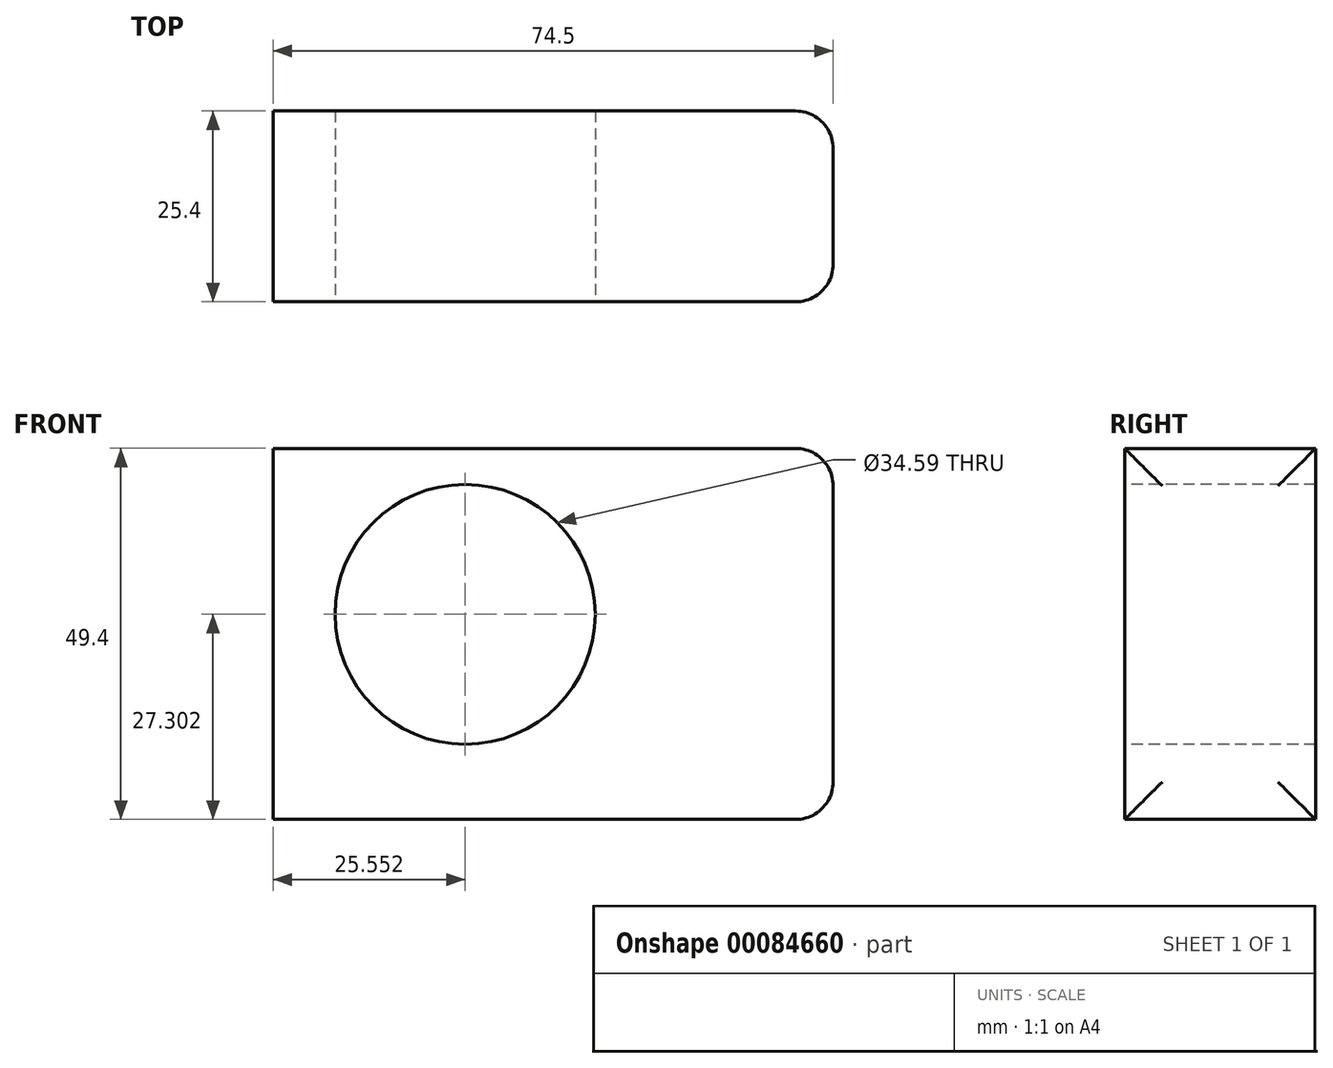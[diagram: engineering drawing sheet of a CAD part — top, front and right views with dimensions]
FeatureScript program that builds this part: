
annotation { "Feature Type Name" : "Feature", "Feature Type Description" : "" }
export const myFeature = defineFeature(function(context is Context, id is Id, definition is map)
    precondition{}
    {
        {
            var Q0;
            Q0=qCreatedBy(makeId("Front.planeOp"),FACE);
            var sketch = newSketch(context, id + "F4", { "sketchPlane" : qUnion([Q0])});
            skLineSegment(sketch, "E0.bottom", {"start": v(32.17, 49.4) * mm, "end": v(-42.33, 49.4) * mm});
            skLineSegment(sketch, "E0.top", {"start": v(32.17, 0) * mm, "end": v(-42.33, 0) * mm});
            skLineSegment(sketch, "E0.left", {"start": v(32.17, 49.4) * mm, "end": v(32.17, 0) * mm});
            skLineSegment(sketch, "E0.right", {"start": v(-42.33, 49.4) * mm, "end": v(-42.33, 0) * mm});
            skSolve(sketch);
        }
        {
            var Q0;
            Q0=makeQuery(id+"F4.imprint","IMPRINT",FACE,{"disambiguationData":[TD([[makeQuery(id+"F4.imprint","IMPRINT",EDGE,{"derivedFrom":sQuery(id+"F4.wireOp",EDGE,"E0.bottom")}),1.0]])]});
            extrude(context, id + "F5", {"entities" : qUnion([Q0]), "depth" : 25.4 * mm});
        }
        {
            var Q0;
            Q0=makeQuery(id+"F5.opExtrude","CAP_FACE",FACE,{"disambiguationData":[OSD([sQuery(id+"F4.wireOp",EDGE,"E0.bottom"),sQuery(id+"F4.wireOp",EDGE,"E0.top"),sQuery(id+"F4.wireOp",EDGE,"E0.left"),sQuery(id+"F4.wireOp",EDGE,"E0.right")])],"isStart":false});
            var sketch = newSketch(context, id + "F0", { "sketchPlane" : qUnion([Q0])});
            skSolve(sketch);
        }
        {
            var Q0;
            Q0=makeQuery(id+"F0.imprint","IMPRINT",FACE,{"disambiguationData":[TD([[makeQuery(id+"F0.imprint","IMPRINT",EDGE,{"derivedFrom":makeQuery(id+"F5.opExtrude","CAP_EDGE",EDGE,{"disambiguationData":[OSD([sQuery(id+"F4.wireOp",EDGE,"E0.bottom")])],"isStart":false})}),1.0]])]});
            var sketch = newSketch(context, id + "F6", { "sketchPlane" : qUnion([Q0])});
            skCircle(sketch, "E1", {"center": v(-16.78, 27.3) * mm, "radius": 17.3 * mm});
            skSolve(sketch);
        }
        {
            var Q0;
            Q0=makeQuery(id+"F6.imprint","IMPRINT",FACE,{"disambiguationData":[TD([[makeQuery(id+"F6.imprint","IMPRINT",EDGE,{"derivedFrom":sQuery(id+"F6.wireOp",EDGE,"E1")}),-1.0]])]});
            var sketch = newSketch(context, id + "F7", { "sketchPlane" : qUnion([Q0])});
            skSolve(sketch);
        }
        {
            var Q0;
            Q0=makeQuery(id+"F5.opExtrude","SWEPT_EDGE",EDGE,{"disambiguationData":[OSD([sQuery(id+"F4.wireOp",EDGE,"E0.bottom"),sQuery(id+"F4.wireOp",EDGE,"E0.left")])]});
            var Q1;
            Q1=makeQuery(id+"F5.opExtrude","CAP_EDGE",EDGE,{"disambiguationData":[OSD([sQuery(id+"F4.wireOp",EDGE,"E0.left")])],"isStart":true});
            var Q2;
            Q2=makeQuery(id+"F5.opExtrude","CAP_EDGE",EDGE,{"disambiguationData":[OSD([sQuery(id+"F4.wireOp",EDGE,"E0.left")])],"isStart":false});
            var Q3;
            Q3=makeQuery(id+"F5.opExtrude","SWEPT_EDGE",EDGE,{"disambiguationData":[OSD([sQuery(id+"F4.wireOp",EDGE,"E0.top"),sQuery(id+"F4.wireOp",EDGE,"E0.left")])]});
            fillet(context, id + "F1", {"entities" : qUnion([Q0, Q1, Q2, Q3]), "radius" : 5 * mm, "tangentPropagation" : true, "allowEdgeOverflow" : false});
        }
        {
            var Q0;
            Q0=makeQuery(id+"F7.imprint","IMPRINT",FACE,{"disambiguationData":[TD([[makeQuery(id+"F7.imprint","IMPRINT",EDGE,{"derivedFrom":makeQuery(id+"F6.imprint","IMPRINT",EDGE,{"derivedFrom":sQuery(id+"F6.wireOp",EDGE,"E1")})}),1.0]])]});
            extrude(context, id + "F2", {"entities" : qUnion([Q0]), "operationType" : NewBodyOperationType.REMOVE, "endBound" : BoundingType.THROUGH_ALL, "oppositeDirection" : true, "depth" : 25.4 * mm});
        }
    });
